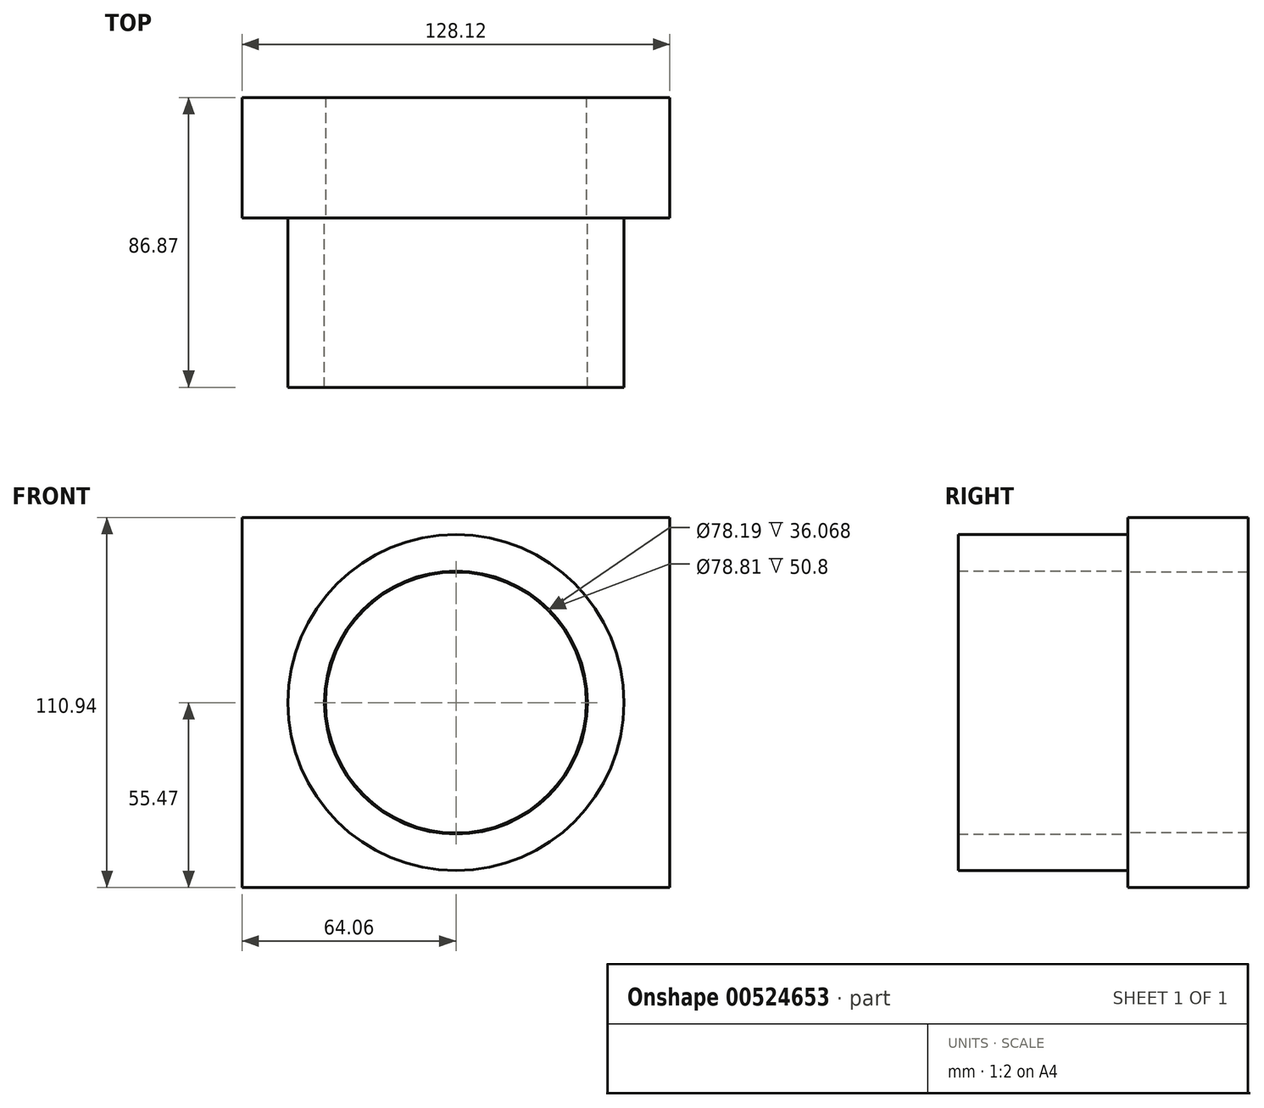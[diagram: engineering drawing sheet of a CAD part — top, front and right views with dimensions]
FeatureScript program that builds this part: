
annotation { "Feature Type Name" : "Feature", "Feature Type Description" : "" }
export const myFeature = defineFeature(function(context is Context, id is Id, definition is map)
    precondition{}
    {
        {
            var Q0;
            Q0=qCreatedBy(makeId("Front.planeOp"),FACE);
            var sketch = newSketch(context, id + "F0", { "sketchPlane" : qUnion([Q0])});
            skLineSegment(sketch, "E0.bottom", {"start": v(64.06, -55.47) * mm, "end": v(-64.06, -55.47) * mm});
            skLineSegment(sketch, "E0.top", {"start": v(64.06, 55.47) * mm, "end": v(-64.06, 55.47) * mm});
            skLineSegment(sketch, "E0.left", {"start": v(64.06, -55.47) * mm, "end": v(64.06, 55.47) * mm});
            skLineSegment(sketch, "E0.right", {"start": v(-64.06, -55.47) * mm, "end": v(-64.06, 55.47) * mm});
            skPoint(sketch, "E0.middle", {"position": v(0, 0) * mm});
            skCircle(sketch, "E1", {"center": v(0, 0) * mm, "radius": 39.1 * mm});
            skSolve(sketch);
        }
        {
            var Q0;
            Q0=makeQuery(id+"F0.imprint","IMPRINT",FACE,{"disambiguationData":[TD([[makeQuery(id+"F0.imprint","IMPRINT",EDGE,{"derivedFrom":sQuery(id+"F0.wireOp",EDGE,"E0.bottom")}),-1.0]])]});
            extrude(context, id + "F1", {"entities" : qUnion([Q0]), "oppositeDirection" : true, "depth" : 36.07 * mm, "offsetDistance" : 25.4 * mm});
        }
        {
            var Q0;
            Q0=qCreatedBy(makeId("Front.planeOp"),FACE);
            var sketch = newSketch(context, id + "F2", { "sketchPlane" : qUnion([Q0])});
            skCircle(sketch, "E2", {"center": v(0, 0) * mm, "radius": 50.36 * mm});
            skCircle(sketch, "E3", {"center": v(0, 0) * mm, "radius": 39.4 * mm});
            skSolve(sketch);
        }
        {
            var Q0;
            Q0=makeQuery(id+"F2.imprint","IMPRINT",FACE,{"disambiguationData":[TD([[makeQuery(id+"F2.imprint","IMPRINT",EDGE,{"derivedFrom":sQuery(id+"F2.wireOp",EDGE,"E2")}),1.0]])]});
            extrude(context, id + "F3", {"entities" : qUnion([Q0]), "operationType" : NewBodyOperationType.ADD, "depth" : 50.8 * mm, "offsetDistance" : 25.4 * mm});
        }
    });
